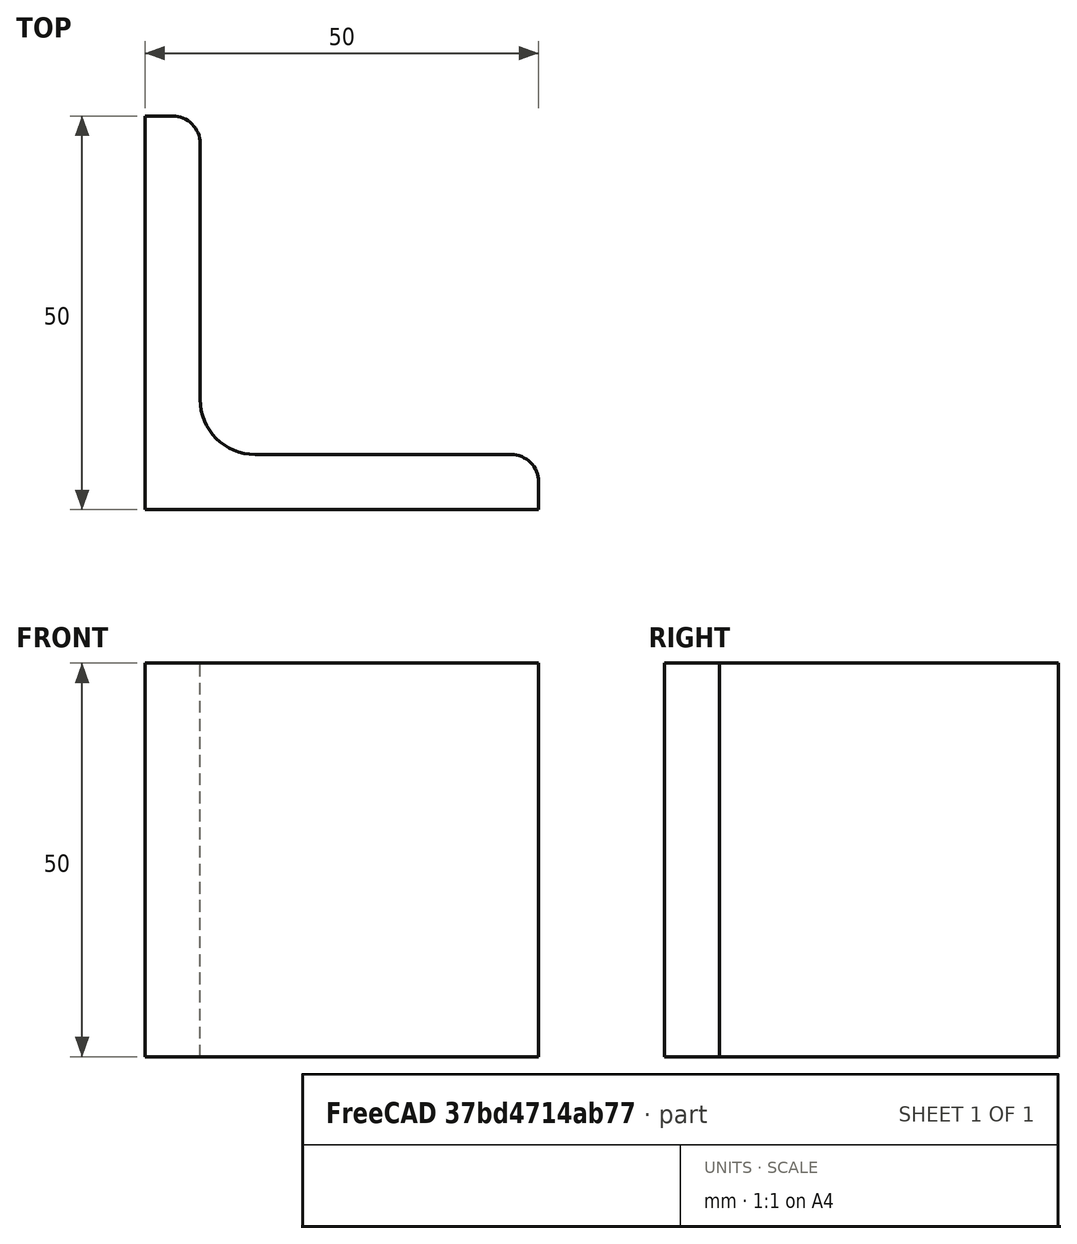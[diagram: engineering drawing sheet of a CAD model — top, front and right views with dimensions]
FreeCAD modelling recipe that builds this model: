
FCSTD DOCUMENT  (FreeCAD 0.15R4671 (Git))
Label: Angle Bar L50x50x7 EN10056 S235JR
License: All rights reserved
LicenseURL: http://en.wikipedia.org/wiki/All_rights_reserved
objects: Sketcher::SketchObject×1, Part::Extrusion×1
note: 2 computed .brp shape members not serialized (recipe doc carries the construction recipe); baked Part::Feature solids carry a one-line shape summary decoded from their .brp

FEATURE [Sketcher::SketchObject] Sketch
  sketch-geometry (9):
    g0: LineSegment StartX=0 StartY=0 StartZ=0 EndX=50 EndY=0 EndZ=0
    g1: LineSegment StartX=50 StartY=0 StartZ=0 EndX=50 EndY=3.5 EndZ=0
    g2: LineSegment StartX=46.5 StartY=7 StartZ=0 EndX=14 EndY=7 EndZ=0
    g3: LineSegment StartX=0 StartY=0 StartZ=0 EndX=0 EndY=50 EndZ=0
    g4: LineSegment StartX=0 StartY=50 StartZ=0 EndX=3.5 EndY=50 EndZ=0
    g5: LineSegment StartX=7 StartY=46.5 StartZ=0 EndX=7 EndY=14 EndZ=0
    g6: ArcOfCircle CenterX=14 CenterY=14 CenterZ=0 NormalX=0 NormalY=0 NormalZ=1 Radius=7 StartAngle=3.14159 EndAngle=4.71239
    g7: ArcOfCircle CenterX=3.5 CenterY=46.5 CenterZ=0 NormalX=0 NormalY=0 NormalZ=1 Radius=3.5 StartAngle=0 EndAngle=1.5708
    g8: ArcOfCircle CenterX=46.5 CenterY=3.5 CenterZ=0 NormalX=0 NormalY=0 NormalZ=1 Radius=3.5 StartAngle=0 EndAngle=1.5708
  constraints (23):
    c: Coincident(g0,g-1)
    c: Horizontal(g0)
    c: Coincident(g1,g0)
    c: Vertical(g1)
    c: Horizontal(g2)
    c: Coincident(g3,g-1)
    c: Vertical(g3)
    c: Coincident(g4,g3)
    c: Horizontal(g4)
    c: Vertical(g5)
    c: Tangent(g5,g6) = -1.5708
    c: Tangent(g2,g6) = 1.5708
    c: Tangent(g4,g7) = 1.5708
    c: Tangent(g5,g7) = 1.5708
    c: Tangent(g2,g8) = -1.5708
    c: Tangent(g1,g8) = -1.5708
    c: DistanceX(g0) = 50
    c: DistanceY(g3) = 50
    c: DistanceY(g0,g2) = 7
    c: DistanceX(g3,g5) = 7
    c: Radius(g6) = 7
    c: Radius(g8) = 3.5
    c: Radius(g7) = 3.5
FEATURE [Part::Extrusion] Extrude  label="Angle Bar L50x50x7 EN10056 S235JR"
  Base = -> Sketch
  Dir = (0,0,50)
  Solid = true
